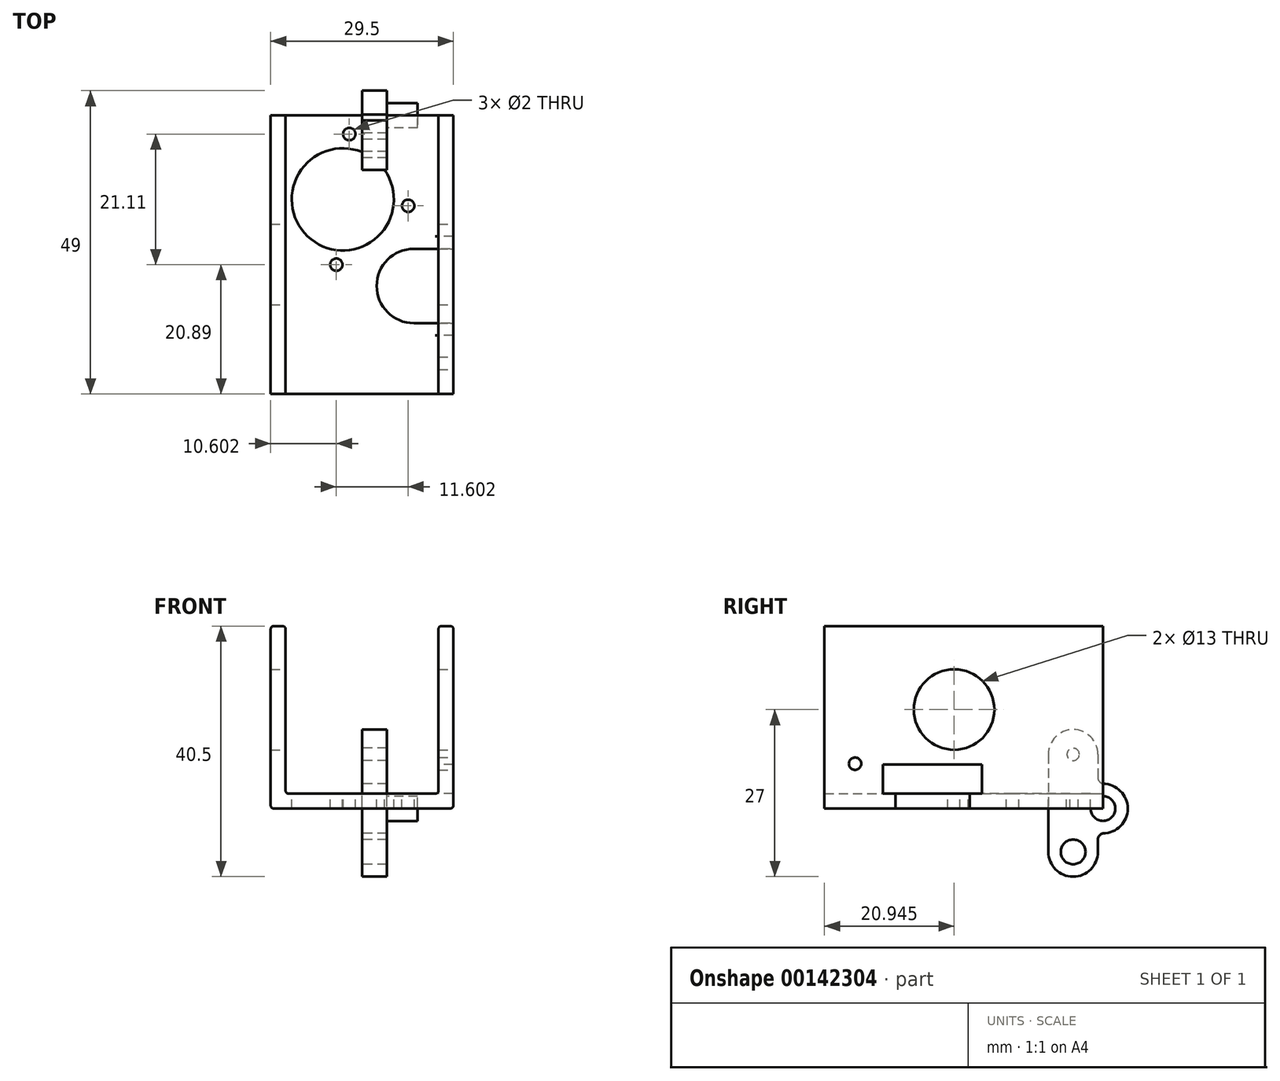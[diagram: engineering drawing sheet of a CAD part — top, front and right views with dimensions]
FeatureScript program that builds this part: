
annotation { "Feature Type Name" : "Feature", "Feature Type Description" : "" }
export const myFeature = defineFeature(function(context is Context, id is Id, definition is map)
    precondition{}
    {
        {
            var Q0;
            Q0=qCreatedBy(makeId("Front.planeOp"),FACE);
            var sketch = newSketch(context, id + "F0", { "sketchPlane" : qUnion([Q0])});
            skLineSegment(sketch, "E0", {"start": v(-14.75, 29.5) * mm, "end": v(-12.35, 29.5) * mm});
            skLineSegment(sketch, "E1", {"start": v(-12.35, 29.5) * mm, "end": v(-12.35, 2.4) * mm});
            skLineSegment(sketch, "E2", {"start": v(-12.35, 2.4) * mm, "end": v(0, 2.4) * mm});
            skLineSegment(sketch, "E3", {"start": v(0, 2.4) * mm, "end": v(0, 0) * mm});
            skLineSegment(sketch, "E4", {"start": v(0, 0) * mm, "end": v(-14.75, 0) * mm});
            skLineSegment(sketch, "E5", {"start": v(-14.75, 0) * mm, "end": v(-14.75, 29.5) * mm});
            skLineSegment(sketch, "E6.MirrorCS", {"start": v(12.35, 29.5) * mm, "end": v(12.35, 2.4) * mm});
            skLineSegment(sketch, "E7.MirrorCS", {"start": v(14.75, 29.5) * mm, "end": v(12.35, 29.5) * mm});
            skLineSegment(sketch, "E8.MirrorCS", {"start": v(14.75, 0) * mm, "end": v(14.75, 29.5) * mm});
            skLineSegment(sketch, "E9.MirrorCS", {"start": v(0, 0) * mm, "end": v(14.75, 0) * mm});
            skLineSegment(sketch, "E10.MirrorCS", {"start": v(12.35, 2.4) * mm, "end": v(0, 2.4) * mm});
            skSolve(sketch);
        }
        {
            var Q0;
            Q0 = qSketchRegion(id + "F0", true);
            extrude(context, id + "F1", {"entities" : qUnion([Q0]), "depth" : 45 * mm});
        }
        {
            var Q0;
            Q0=makeQuery(id+"F1.opExtrude","SWEPT_EDGE",EDGE,{"disambiguationData":[OSD([sQuery(id+"F0.wireOp",EDGE,"E0"),sQuery(id+"F0.wireOp",EDGE,"E5")])]});
            var Q1;
            Q1=makeQuery(id+"F1.opExtrude","SWEPT_EDGE",EDGE,{"disambiguationData":[OSD([sQuery(id+"F0.wireOp",EDGE,"E0"),sQuery(id+"F0.wireOp",EDGE,"E1")])]});
            var Q2;
            Q2=makeQuery(id+"F1.opExtrude","SWEPT_EDGE",EDGE,{"disambiguationData":[OSD([sQuery(id+"F0.wireOp",EDGE,"E6.MirrorCS"),sQuery(id+"F0.wireOp",EDGE,"E7.MirrorCS")])]});
            var Q3;
            Q3=makeQuery(id+"F1.opExtrude","SWEPT_EDGE",EDGE,{"disambiguationData":[OSD([sQuery(id+"F0.wireOp",EDGE,"E7.MirrorCS"),sQuery(id+"F0.wireOp",EDGE,"E8.MirrorCS")])]});
            var Q4;
            Q4=makeQuery(id+"F1.opExtrude","SWEPT_EDGE",EDGE,{"disambiguationData":[OSD([sQuery(id+"F0.wireOp",EDGE,"E8.MirrorCS"),sQuery(id+"F0.wireOp",EDGE,"E9.MirrorCS")])]});
            var Q5;
            Q5=makeQuery(id+"F1.opExtrude","SWEPT_EDGE",EDGE,{"disambiguationData":[OSD([sQuery(id+"F0.wireOp",EDGE,"E4"),sQuery(id+"F0.wireOp",EDGE,"E5")])]});
            var Q6;
            Q6=makeQuery(id+"F1.opExtrude","SWEPT_EDGE",EDGE,{"disambiguationData":[OSD([sQuery(id+"F0.wireOp",EDGE,"E1"),sQuery(id+"F0.wireOp",EDGE,"E2")])]});
            var Q7;
            Q7=makeQuery(id+"F1.opExtrude","SWEPT_EDGE",EDGE,{"disambiguationData":[OSD([sQuery(id+"F0.wireOp",EDGE,"E6.MirrorCS"),sQuery(id+"F0.wireOp",EDGE,"E10.MirrorCS")])]});
            fillet(context, id + "F2", {"entities" : qUnion([Q0, Q1, Q2, Q3, Q4, Q5, Q6, Q7]), "radius" : 0.5 * mm, "tangentPropagation" : true, "allowEdgeOverflow" : false});
        }
        {
            var Q0;
            Q0=makeQuery(id+"F1.opExtrude","SWEPT_FACE",FACE,{"disambiguationData":[OSD([sQuery(id+"F0.wireOp",EDGE,"E2"),sQuery(id+"F0.wireOp",EDGE,"E10.MirrorCS")])]});
            var sketch = newSketch(context, id + "F3", { "sketchPlane" : qUnion([Q0])});
            skCircle(sketch, "E11", {"center": v(-3.1, -13.55) * mm, "radius": 8.25 * mm});
            skCircle(sketch, "E12.1.0", {"center": v(-4.15, -24.1) * mm, "radius": 1 * mm});
            skCircle(sketch, "E12.2.0", {"center": v(7.45, -14.6) * mm, "radius": 1 * mm});
            skCircle(sketch, "E12.3.0", {"center": v(-2.05, -3) * mm, "radius": 1 * mm});
            skArc(sketch, "E13", {"start": v(8.37, -21.55) * mm, "mid": v(2.37, -27.55) * mm, "end": v(8.37, -33.55) * mm});
            skLineSegment(sketch, "E14", {"start": v(-3.1, -13.55) * mm, "end": v(8.37, -27.55) * mm, "construction": true});
            skLineSegment(sketch, "E15", {"start": v(-4.15, -24.1) * mm, "end": v(7.45, -14.6) * mm, "construction": true});
            skLineSegment(sketch, "E16.0", {"start": v(14.75, 0) * mm, "end": v(14.75, -45) * mm});
            skLineSegment(sketch, "E17", {"start": v(8.37, -33.55) * mm, "end": v(14.75, -33.55) * mm});
            skLineSegment(sketch, "E18", {"start": v(8.37, -21.55) * mm, "end": v(14.75, -21.55) * mm});
            skCircle(sketch, "E19", {"center": v(8.37, -27.55) * mm, "radius": 8 * mm});
            skSolve(sketch);
        }
        {
            var Q0;
            Q0=makeQuery(id+"F3.imprint","IMPRINT",FACE,{"disambiguationData":[TD([[makeQuery(id+"F3.imprint","IMPRINT",EDGE,{"derivedFrom":sQuery(id+"F3.wireOp",EDGE,"E11")}),1.0]])]});
            var Q1;
            Q1=makeQuery(id+"F3.imprint","IMPRINT",FACE,{"disambiguationData":[TD([[makeQuery(id+"F3.imprint","IMPRINT",EDGE,{"derivedFrom":sQuery(id+"F3.wireOp",EDGE,"E12.1.0")}),1.0]])]});
            var Q2;
            Q2=makeQuery(id+"F3.imprint","IMPRINT",FACE,{"disambiguationData":[TD([[makeQuery(id+"F3.imprint","IMPRINT",EDGE,{"derivedFrom":sQuery(id+"F3.wireOp",EDGE,"E12.2.0")}),1.0]])]});
            var Q3;
            Q3=makeQuery(id+"F3.imprint","IMPRINT",FACE,{"disambiguationData":[TD([[makeQuery(id+"F3.imprint","IMPRINT",EDGE,{"derivedFrom":sQuery(id+"F3.wireOp",EDGE,"E12.3.0")}),1.0]])]});
            var Q4;
            {var subQ0=sQuery(id+"F3.wireOp",EDGE,"E18");var subQ1=sQuery(id+"F3.wireOp",EDGE,"E16.0");var subQ2=makeQuery(id+"F3.imprint","INTERSECT",VERTEX,{"derivedFrom":[subQ1,subQ0]});Q4=makeQuery(id+"F3.imprint","IMPRINT",FACE,{"disambiguationData":[TD([[makeQuery(id+"F3.imprint","IMPRINT",EDGE,{"disambiguationData":[TD([[subQ2,-1.0]])],"derivedFrom":subQ1}),-1.0]])]});}
            var Q5;
            {var subQ0=sQuery(id+"F3.wireOp",EDGE,"E17");var subQ1=sQuery(id+"F3.wireOp",EDGE,"E16.0");var subQ2=makeQuery(id+"F3.imprint","INTERSECT",VERTEX,{"derivedFrom":[subQ1,subQ0]});Q5=makeQuery(id+"F3.imprint","IMPRINT",FACE,{"disambiguationData":[TD([[makeQuery(id+"F3.imprint","IMPRINT",EDGE,{"disambiguationData":[TD([[subQ2,1.0]])],"derivedFrom":subQ1}),-1.0]])]});}
            var Q6;
            {var subQ0=sQuery(id+"F3.wireOp",EDGE,"E13");Q6=makeQuery(id+"F3.imprint","IMPRINT",FACE,{"disambiguationData":[TD([[makeQuery(id+"F3.imprint","IMPRINT",EDGE,{"derivedFrom":subQ0}),1.0]])]});}
            var Q7;
            {var subQ0=sQuery(id+"F3.wireOp",EDGE,"E19");var subQ9=sQuery(id+"F3.wireOp",EDGE,"E16.0");var subQ10=makeQuery(id+"F3.imprint","INTERSECT",VERTEX,{"disambiguationData":[OD(0.0)],"derivedFrom":[subQ9,subQ0]});Q7=makeQuery(id+"F3.imprint","IMPRINT",FACE,{"disambiguationData":[TD([[makeQuery(id+"F3.imprint","IMPRINT",EDGE,{"disambiguationData":[TD([[subQ10,-1.0]])],"derivedFrom":subQ9}),-1.0]])]});}
            extrude(context, id + "F4", {"entities" : qUnion([Q0, Q1, Q2, Q3, Q4, Q5, Q6, Q7]), "operationType" : NewBodyOperationType.REMOVE, "endBound" : BoundingType.THROUGH_ALL, "oppositeDirection" : true, "depth" : 25 * mm});
        }
        {
            var Q0;
            Q0=makeQuery(id+"F1.opExtrude","SWEPT_FACE",FACE,{"disambiguationData":[OSD([sQuery(id+"F0.wireOp",EDGE,"E8.MirrorCS")])]});
            var sketch = newSketch(context, id + "F5", { "sketchPlane" : qUnion([Q0])});
            skCircle(sketch, "E20", {"center": v(-24.05, 16) * mm, "radius": 6.5 * mm});
            skCircle(sketch, "E21", {"center": v(-40.05, 7.25) * mm, "radius": 1 * mm});
            skSolve(sketch);
        }
        {
            var Q0;
            Q0=makeQuery(id+"F5.imprint","IMPRINT",FACE,{"disambiguationData":[TD([[makeQuery(id+"F5.imprint","IMPRINT",EDGE,{"derivedFrom":sQuery(id+"F5.wireOp",EDGE,"E20")}),1.0]])]});
            extrude(context, id + "F6", {"entities" : qUnion([Q0]), "operationType" : NewBodyOperationType.REMOVE, "endBound" : BoundingType.THROUGH_ALL, "oppositeDirection" : true, "depth" : 25 * mm});
        }
        {
            var Q0;
            Q0=makeQuery(id+"F1.opExtrude","SWEPT_FACE",FACE,{"disambiguationData":[OSD([sQuery(id+"F0.wireOp",EDGE,"E6.MirrorCS")])]});
            var sketch = newSketch(context, id + "F7", { "sketchPlane" : qUnion([Q0])});
            skPoint(sketch, "E22.0", {"position": v(27.55, 2.4) * mm});
            skLineSegment(sketch, "E23", {"start": v(27.55, 2.4) * mm, "end": v(35.55, 2.4) * mm});
            skLineSegment(sketch, "E24", {"start": v(35.55, 2.4) * mm, "end": v(35.55, 7.1) * mm});
            skLineSegment(sketch, "E25", {"start": v(35.55, 7.1) * mm, "end": v(19.55, 7.1) * mm});
            skLineSegment(sketch, "E26", {"start": v(19.55, 7.1) * mm, "end": v(19.55, 2.4) * mm});
            skLineSegment(sketch, "E27", {"start": v(19.55, 2.4) * mm, "end": v(27.55, 2.4) * mm});
            skSolve(sketch);
        }
        {
            var Q0;
            Q0 = qSketchRegion(id + "F7", true);
            extrude(context, id + "F8", {"entities" : qUnion([Q0]), "operationType" : NewBodyOperationType.REMOVE, "endBound" : BoundingType.THROUGH_ALL, "oppositeDirection" : true, "depth" : 25 * mm, "hasSecondDirection" : true, "secondDirectionOppositeDirection" : false, "secondDirectionDepth" : 3 * mm});
        }
        {
            var Q0;
            Q0=qCreatedBy(makeId("Right.planeOp"),FACE);
            var sketch = newSketch(context, id + "F9", { "sketchPlane" : qUnion([Q0])});
            skCircle(sketch, "E28", {"center": v(0, 0) * mm, "radius": 2 * mm});
            skCircle(sketch, "E29", {"center": v(-4.82, 8.76) * mm, "radius": 1 * mm});
            skCircle(sketch, "E30", {"center": v(-4.82, -7) * mm, "radius": 2 * mm});
            skLineSegment(sketch, "E31", {"start": v(-8.82, 8.76) * mm, "end": v(-8.82, -7) * mm});
            skArc(sketch, "E32", {"start": v(-0.82, 8.76) * mm, "mid": v(-4.82, 12.76) * mm, "end": v(-8.82, 8.76) * mm});
            skArc(sketch, "E33", {"start": v(-8.82, -7) * mm, "mid": v(-4.82, -11) * mm, "end": v(-0.82, -7) * mm});
            skArc(sketch, "E34", {"start": v(0, -4) * mm, "mid": v(4, 0) * mm, "end": v(0, 4) * mm});
            skLineSegment(sketch, "E35", {"start": v(-0.82, 8.76) * mm, "end": v(-0.82, 5) * mm});
            skLineSegment(sketch, "E36", {"start": v(0.18, 4) * mm, "end": v(0, 4) * mm});
            skLineSegment(sketch, "E37", {"start": v(0.18, -4) * mm, "end": v(0, -4) * mm});
            skLineSegment(sketch, "E38.trimOffspring", {"start": v(-0.82, -5) * mm, "end": v(-0.82, -7) * mm});
            skPoint(sketch, "E39.visualSharp", {"position": v(-0.82, 4) * mm});
            skArc(sketch, "E39.filletArc", {"start": v(-0.82, 5) * mm, "mid": v(-0.53, 4.3) * mm, "end": v(0.18, 4) * mm});
            skPoint(sketch, "E40.visualSharp", {"position": v(-0.82, -4) * mm});
            skArc(sketch, "E40.filletArc", {"start": v(0.18, -4) * mm, "mid": v(-0.53, -4.3) * mm, "end": v(-0.82, -5) * mm});
            skSolve(sketch);
        }
        {
            var Q0;
            Q0 = qSketchRegion(id + "F9", true);
            var Q1;
            Q1=makeQuery(id+"F9.imprint","IMPRINT",FACE,{"disambiguationData":[TD([[makeQuery(id+"F9.imprint","IMPRINT",EDGE,{"derivedFrom":sQuery(id+"F9.wireOp",EDGE,"E28")}),1.0]])]});
            extrude(context, id + "F10", {"entities" : qUnion([Q0, Q1]), "depth" : 4 * mm});
        }
        {
            var Q0;
            Q0=makeQuery(id+"F9.imprint","IMPRINT",FACE,{"disambiguationData":[TD([[makeQuery(id+"F9.imprint","IMPRINT",EDGE,{"derivedFrom":sQuery(id+"F9.wireOp",EDGE,"E28")}),1.0]])]});
            extrude(context, id + "F11", {"entities" : qUnion([Q0]), "operationType" : NewBodyOperationType.ADD, "depth" : 9 * mm});
        }
        {
            var Q0;
            Q0=makeQuery(id+"F5.imprint","IMPRINT",FACE,{"disambiguationData":[TD([[makeQuery(id+"F5.imprint","IMPRINT",EDGE,{"derivedFrom":sQuery(id+"F5.wireOp",EDGE,"E21")}),1.0]])]});
            extrude(context, id + "F12", {"entities" : qUnion([Q0]), "operationType" : NewBodyOperationType.REMOVE, "oppositeDirection" : true, "depth" : 5 * mm});
        }
    });
